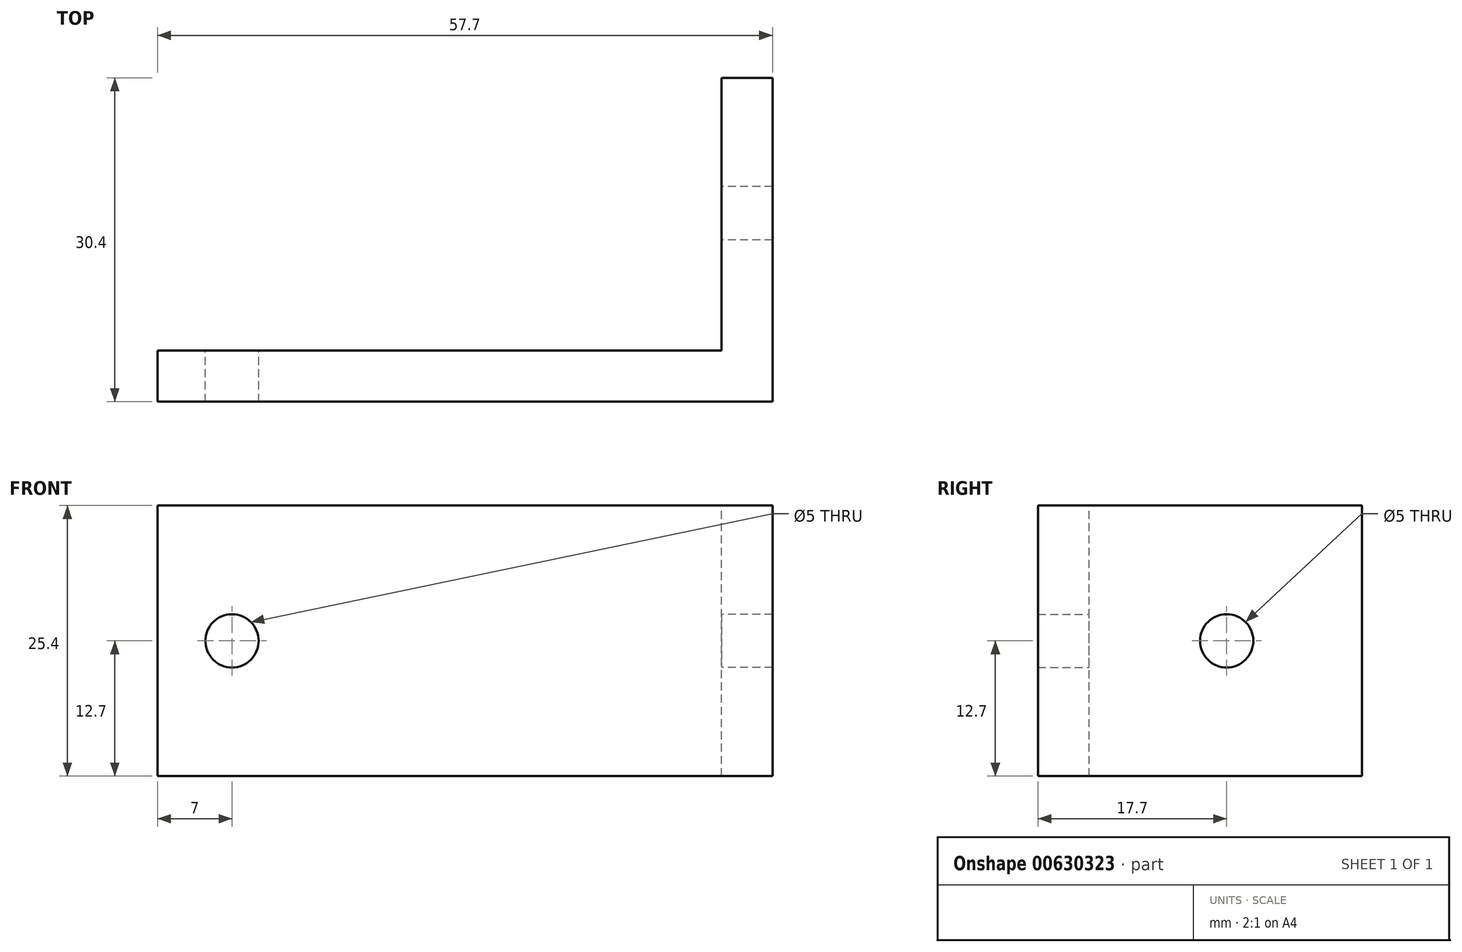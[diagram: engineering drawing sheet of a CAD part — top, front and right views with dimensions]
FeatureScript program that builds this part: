
annotation { "Feature Type Name" : "Feature", "Feature Type Description" : "" }
export const myFeature = defineFeature(function(context is Context, id is Id, definition is map)
    precondition{}
    {
        {
            var Q0;
            Q0=qCreatedBy(makeId("Top.planeOp"),FACE);
            var sketch = newSketch(context, id + "F0", { "sketchPlane" : qUnion([Q0])});
            skLineSegment(sketch, "E0.top", {"start": v(0, 25.4) * mm, "end": v(5, 25.4) * mm});
            skLineSegment(sketch, "E0.left", {"start": v(0, 0) * mm, "end": v(0, 25.4) * mm});
            skLineSegment(sketch, "E0.right", {"start": v(5, 0) * mm, "end": v(5, 25.4) * mm});
            skLineSegment(sketch, "E1.bottom", {"start": v(0, 0) * mm, "end": v(-25.4, 0) * mm});
            skLineSegment(sketch, "E1.top", {"start": v(5, -5) * mm, "end": v(-25.4, -5) * mm});
            skLineSegment(sketch, "E1.left", {"start": v(5, 0) * mm, "end": v(5, -5) * mm});
            skLineSegment(sketch, "E1.right", {"start": v(-25.4, 0) * mm, "end": v(-25.4, -5) * mm});
            skLineSegment(sketch, "E2.bottom", {"start": v(-25.4, -5) * mm, "end": v(-52.7, -5) * mm});
            skLineSegment(sketch, "E2.top", {"start": v(-25.4, 0) * mm, "end": v(-52.7, 0) * mm});
            skLineSegment(sketch, "E2.left", {"start": v(-25.4, -5) * mm, "end": v(-25.4, 0) * mm, "construction": true});
            skLineSegment(sketch, "E2.right", {"start": v(-52.7, -5) * mm, "end": v(-52.7, 0) * mm});
            skLineSegment(sketch, "E3", {"start": v(-12.7, 0) * mm, "end": v(-12.7, -5) * mm, "construction": true});
            skLineSegment(sketch, "E4", {"start": v(0, 12.7) * mm, "end": v(5, 12.7) * mm, "construction": true});
            skSolve(sketch);
        }
        {
            var Q0;
            Q0 = qSketchRegion(id + "F0", true);
            extrude(context, id + "F1", {"entities" : qUnion([Q0]), "depth" : 25.4 * mm, "offsetDistance" : 25.4 * mm});
        }
        {
            var Q0;
            Q0=makeQuery(id+"F1.opExtrude","SWEPT_FACE",FACE,{"disambiguationData":[OSD([sQuery(id+"F0.wireOp",EDGE,"E0.left")])]});
            var sketch = newSketch(context, id + "F2", { "sketchPlane" : qUnion([Q0])});
            skLineSegment(sketch, "E5", {"start": v(0, 25.4) * mm, "end": v(-25.4, 0) * mm, "construction": true});
            skCircle(sketch, "E6", {"center": v(-12.7, 12.7) * mm, "radius": 2.5 * mm});
            skSolve(sketch);
        }
        {
            var Q0;
            Q0 = qSketchRegion(id + "F2", true);
            extrude(context, id + "F3", {"entities" : qUnion([Q0]), "operationType" : NewBodyOperationType.REMOVE, "endBound" : BoundingType.THROUGH_ALL, "oppositeDirection" : true, "depth" : 25.4 * mm, "offsetDistance" : 25.4 * mm});
        }
        {
            var Q0;
            Q0=makeQuery(id+"F1.opExtrude","SWEPT_FACE",FACE,{"disambiguationData":[OSD([sQuery(id+"F0.wireOp",EDGE,"E1.bottom"),sQuery(id+"F0.wireOp",EDGE,"E2.top")])]});
            var sketch = newSketch(context, id + "F4", { "sketchPlane" : qUnion([Q0])});
            skLineSegment(sketch, "E7", {"start": v(52.7, 12.7) * mm, "end": v(0, 12.7) * mm, "construction": true});
            skCircle(sketch, "E8", {"center": v(45.7, 12.7) * mm, "radius": 2.5 * mm});
            skSolve(sketch);
        }
        {
            var Q0;
            Q0 = qSketchRegion(id + "F4", true);
            extrude(context, id + "F5", {"entities" : qUnion([Q0]), "operationType" : NewBodyOperationType.REMOVE, "endBound" : BoundingType.THROUGH_ALL, "oppositeDirection" : true, "depth" : 25.4 * mm, "offsetDistance" : 25.4 * mm});
        }
        {
            var Q0;
            Q0=makeQuery(id+"F1.opExtrude","CAP_FACE",FACE,{"disambiguationData":[OSD([sQuery(id+"F0.wireOp",EDGE,"E0.top"),sQuery(id+"F0.wireOp",EDGE,"E0.left"),sQuery(id+"F0.wireOp",EDGE,"E0.right"),sQuery(id+"F0.wireOp",EDGE,"E1.bottom"),sQuery(id+"F0.wireOp",EDGE,"E1.top"),sQuery(id+"F0.wireOp",EDGE,"E1.left"),sQuery(id+"F0.wireOp",EDGE,"E2.bottom"),sQuery(id+"F0.wireOp",EDGE,"E2.top"),sQuery(id+"F0.wireOp",EDGE,"E2.right")])],"isStart":false});
            var sketch = newSketch(context, id + "F6", { "sketchPlane" : qUnion([Q0])});
            skLineSegment(sketch, "E9.bottom", {"start": v(-52.7, 0) * mm, "end": v(0, 0) * mm});
            skLineSegment(sketch, "E9.top", {"start": v(-52.7, -0.2) * mm, "end": v(0, -0.2) * mm});
            skLineSegment(sketch, "E9.left", {"start": v(-52.7, 0) * mm, "end": v(-52.7, -0.2) * mm});
            skLineSegment(sketch, "E9.right", {"start": v(0, 0) * mm, "end": v(0, -0.2) * mm});
            skLineSegment(sketch, "E10.bottom", {"start": v(0, 25.4) * mm, "end": v(0.2, 25.4) * mm});
            skLineSegment(sketch, "E10.top", {"start": v(0, -0.2) * mm, "end": v(0.2, -0.2) * mm});
            skLineSegment(sketch, "E10.left", {"start": v(0, 25.4) * mm, "end": v(0, -0.2) * mm});
            skLineSegment(sketch, "E10.right", {"start": v(0.2, 25.4) * mm, "end": v(0.2, -0.2) * mm});
            skSolve(sketch);
        }
        {
            var Q0;
            Q0 = qSketchRegion(id + "F6", true);
            extrude(context, id + "F7", {"entities" : qUnion([Q0]), "operationType" : NewBodyOperationType.REMOVE, "endBound" : BoundingType.THROUGH_ALL, "oppositeDirection" : true, "depth" : 25.4 * mm, "offsetDistance" : 25.4 * mm});
        }
    });
